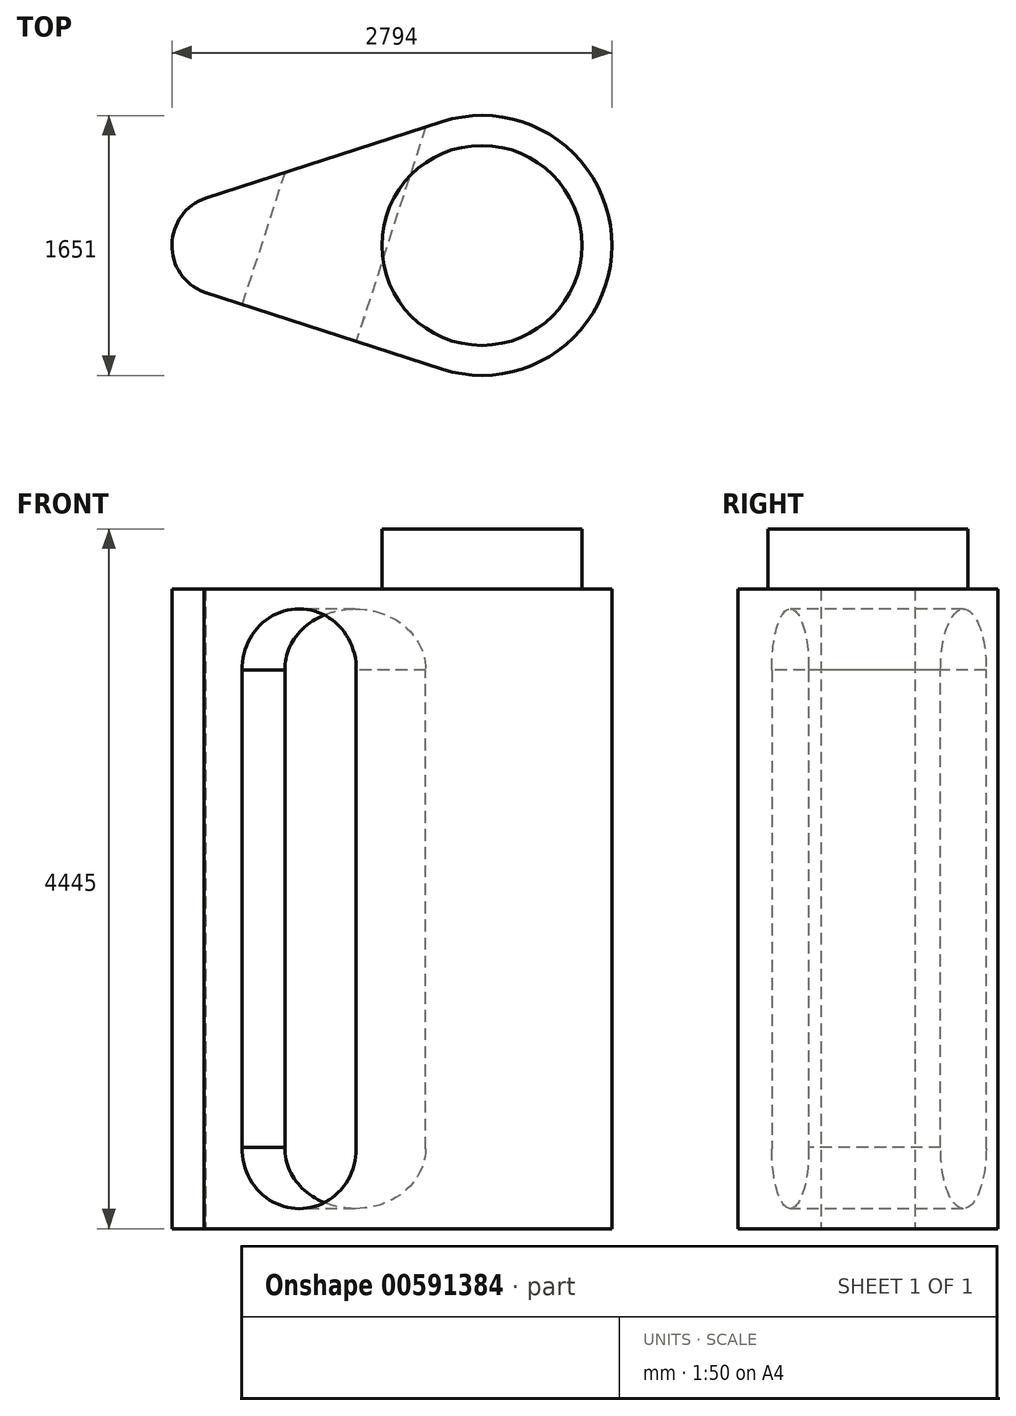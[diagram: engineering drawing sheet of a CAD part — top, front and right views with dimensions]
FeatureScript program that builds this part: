
annotation { "Feature Type Name" : "Feature", "Feature Type Description" : "" }
export const myFeature = defineFeature(function(context is Context, id is Id, definition is map)
    precondition{}
    {
        {
            var Q0;
            Q0=qCreatedBy(makeId("Top.planeOp"),FACE);
            var sketch = newSketch(context, id + "F0", { "sketchPlane" : qUnion([Q0])});
            skArc(sketch, "E0", {"start": v(-254.2, -785.38) * mm, "mid": v(825.5, -0.1) * mm, "end": v(-254.03, 785.44) * mm});
            skArc(sketch, "E1", {"start": v(-1754.9, 300.02) * mm, "mid": v(-1968.3, -11.37) * mm, "end": v(-1733.16, -306.69) * mm});
            skLineSegment(sketch, "E2", {"start": v(-1754.9, 300.02) * mm, "end": v(-254.03, 785.44) * mm});
            skLineSegment(sketch, "E3", {"start": v(-1764.13, -296.66) * mm, "end": v(-254.2, -785.38) * mm});
            skSolve(sketch);
        }
        {
            var Q0;
            {var subQ5=sQuery(id+"F0.wireOp",EDGE,"E0");Q0=makeQuery(id+"F0.imprint","IMPRINT",FACE,{"disambiguationData":[TD([[makeQuery(id+"F0.imprint","IMPRINT",EDGE,{"derivedFrom":subQ5}),1.0]])]});}
            extrude(context, id + "F1", {"entities" : qUnion([Q0]), "depth" : 4064 * mm, "offsetDistance" : 25.4 * mm});
        }
        {
            var Q0;
            Q0=makeQuery(id+"F1.opExtrude","SWEPT_FACE",FACE,{"disambiguationData":[OSD([sQuery(id+"F0.wireOp",EDGE,"E3")])]});
            var sketch = newSketch(context, id + "F2", { "sketchPlane" : qUnion([Q0])});
            skArc(sketch, "E4", {"start": v(-571.24, 3547.08) * mm, "mid": v(-951.78, 3937) * mm, "end": v(-1333.04, 3547.8) * mm});
            skArc(sketch, "E5", {"start": v(-1333.04, 516.2) * mm, "mid": v(-956.23, 127.02) * mm, "end": v(-571.13, 508.01) * mm});
            skLineSegment(sketch, "E6", {"start": v(-1333.04, 3564.2) * mm, "end": v(-1333.04, 499.8) * mm});
            skLineSegment(sketch, "E7", {"start": v(-571.24, 3564.95) * mm, "end": v(-571.13, 508.01) * mm});
            skSolve(sketch);
        }
        {
            var Q0;
            Q0 = qSketchRegion(id + "F2", true);
            extrude(context, id + "F3", {"entities" : qUnion([Q0]), "operationType" : NewBodyOperationType.REMOVE, "endBound" : BoundingType.THROUGH_ALL, "oppositeDirection" : true, "depth" : 25.4 * mm, "offsetDistance" : 25.4 * mm});
        }
        {
            var Q0;
            Q0=makeQuery(id+"F1.opExtrude","CAP_FACE",FACE,{"disambiguationData":[OSD([sQuery(id+"F0.wireOp",EDGE,"E0"),sQuery(id+"F0.wireOp",EDGE,"E1"),sQuery(id+"F0.wireOp",EDGE,"E2"),sQuery(id+"F0.wireOp",EDGE,"E3")])],"isStart":false});
            var sketch = newSketch(context, id + "F4", { "sketchPlane" : qUnion([Q0])});
            skCircle(sketch, "E8", {"center": v(0, 0) * mm, "radius": 635 * mm});
            skSolve(sketch);
        }
        {
            var Q0;
            Q0=makeQuery(id+"F4.imprint","IMPRINT",FACE,{"disambiguationData":[TD([[makeQuery(id+"F4.imprint","IMPRINT",EDGE,{"derivedFrom":sQuery(id+"F4.wireOp",EDGE,"E8")}),1.0]])]});
            extrude(context, id + "F5", {"entities" : qUnion([Q0]), "operationType" : NewBodyOperationType.ADD, "depth" : 381 * mm, "offsetDistance" : 25.4 * mm});
        }
    });
